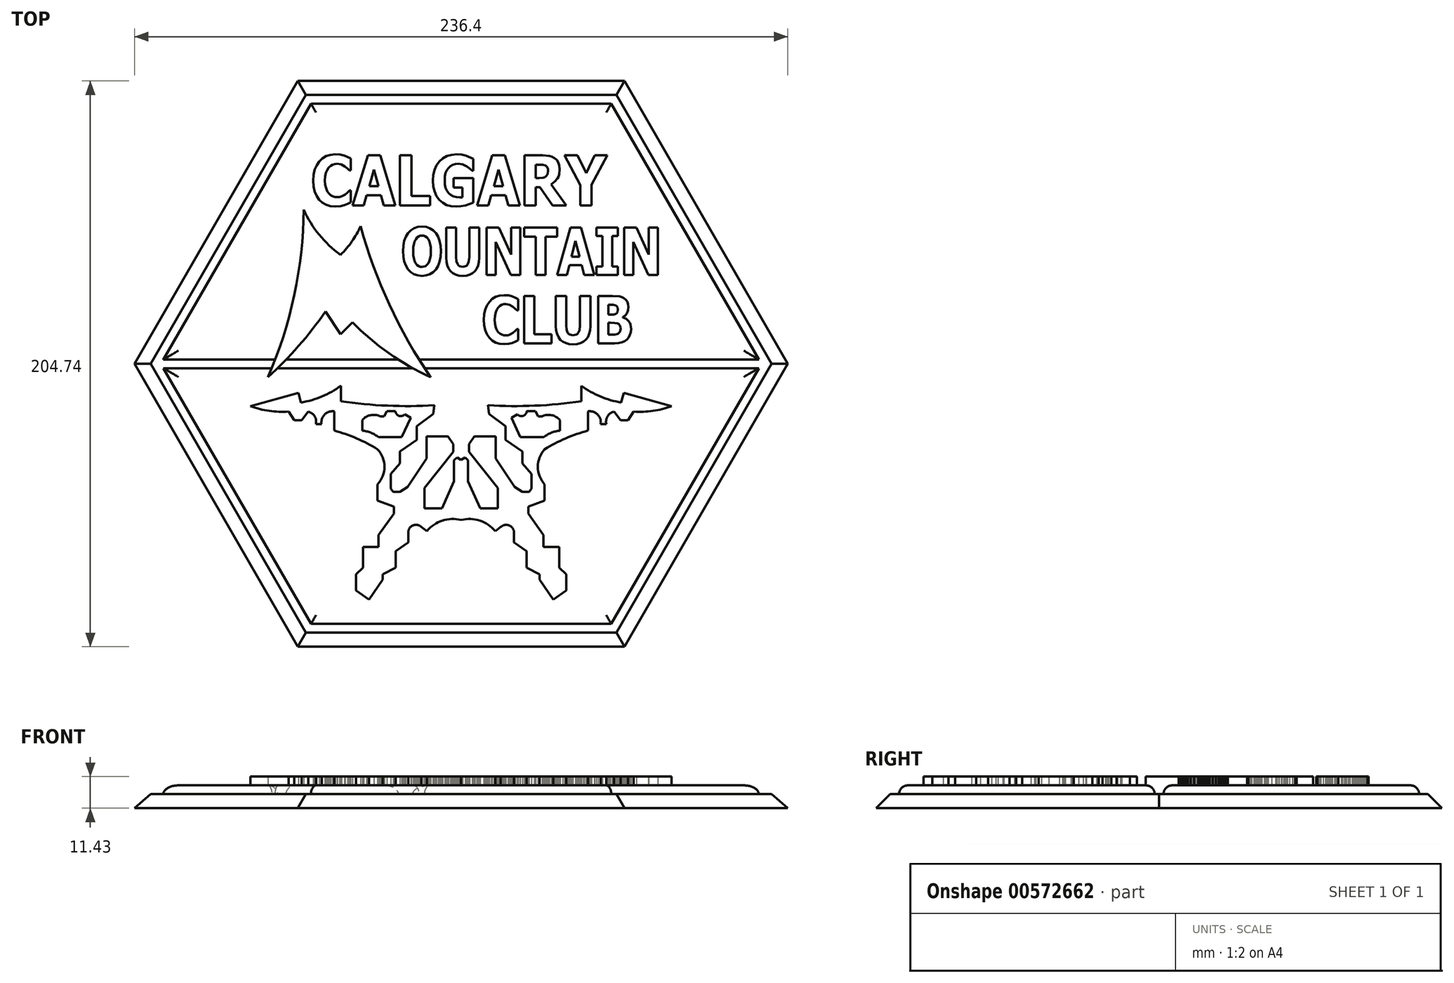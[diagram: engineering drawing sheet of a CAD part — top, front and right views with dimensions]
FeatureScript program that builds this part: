
annotation { "Feature Type Name" : "Feature", "Feature Type Description" : "" }
export const myFeature = defineFeature(function(context is Context, id is Id, definition is map)
    precondition{}
    {
        {
            var Q0;
            Q0=qCreatedBy(makeId("Top.planeOp"),FACE);
            var sketch = newSketch(context, id + "F0", { "sketchPlane" : qUnion([Q0])});
            skLineSegment(sketch, "E0", {"start": v(63.5, 109.99) * mm, "end": v(-63.5, 109.99) * mm});
            skLineSegment(sketch, "E1", {"start": v(63.5, 109.99) * mm, "end": v(127, 0) * mm});
            skLineSegment(sketch, "E2.1.0", {"start": v(-127, 0) * mm, "end": v(-63.5, 109.99) * mm});
            skLineSegment(sketch, "E2.1.1", {"start": v(-127, 0) * mm, "end": v(-63.5, -109.99) * mm});
            skLineSegment(sketch, "E2.2.0", {"start": v(63.5, -109.99) * mm, "end": v(-63.5, -109.99) * mm});
            skLineSegment(sketch, "E2.2.1", {"start": v(63.5, -109.99) * mm, "end": v(127, 0) * mm});
            skPoint(sketch, "E2.center", {"position": v(0, 0) * mm});
            skLineSegment(sketch, "E3", {"start": v(127, 0) * mm, "end": v(-127, 0) * mm, "construction": true});
            skSolve(sketch);
        }
        {
            var Q0;
            Q0=makeQuery(id+"F0.imprint","IMPRINT",FACE,{"disambiguationData":[TD([[makeQuery(id+"F0.imprint","IMPRINT",EDGE,{"derivedFrom":sQuery(id+"F0.wireOp",EDGE,"E0")}),1.0]])]});
            extrude(context, id + "F1", {"entities" : qUnion([Q0]), "depth" : 5.08 * mm, "offsetDistance" : 25.4 * mm});
        }
        {
            var Q0;
            Q0=makeQuery(id+"F1.opExtrude","CAP_EDGE",EDGE,{"disambiguationData":[OSD([sQuery(id+"F0.wireOp",EDGE,"E2.2.0")])],"isStart":false});
            var Q1;
            Q1=makeQuery(id+"F1.opExtrude","CAP_EDGE",EDGE,{"disambiguationData":[OSD([sQuery(id+"F0.wireOp",EDGE,"E2.1.1")])],"isStart":false});
            var Q2;
            Q2=makeQuery(id+"F1.opExtrude","CAP_EDGE",EDGE,{"disambiguationData":[OSD([sQuery(id+"F0.wireOp",EDGE,"E2.1.0")])],"isStart":false});
            var Q3;
            Q3=makeQuery(id+"F1.opExtrude","CAP_EDGE",EDGE,{"disambiguationData":[OSD([sQuery(id+"F0.wireOp",EDGE,"E0")])],"isStart":false});
            var Q4;
            Q4=makeQuery(id+"F1.opExtrude","CAP_EDGE",EDGE,{"disambiguationData":[OSD([sQuery(id+"F0.wireOp",EDGE,"E1")])],"isStart":false});
            var Q5;
            Q5=makeQuery(id+"F1.opExtrude","CAP_EDGE",EDGE,{"disambiguationData":[OSD([sQuery(id+"F0.wireOp",EDGE,"E2.2.1")])],"isStart":false});
            chamfer(context, id + "F2", {"entities" : qUnion([Q0, Q1, Q2, Q3, Q4, Q5]), "width" : 12.7 * mm, "tangentPropagation" : true});
        }
        {
            var Q0;
            Q0=makeQuery(id+"F1.opExtrude","CAP_FACE",FACE,{"disambiguationData":[OSD([sQuery(id+"F0.wireOp",EDGE,"E0"),sQuery(id+"F0.wireOp",EDGE,"E1"),sQuery(id+"F0.wireOp",EDGE,"E2.1.0"),sQuery(id+"F0.wireOp",EDGE,"E2.1.1"),sQuery(id+"F0.wireOp",EDGE,"E2.2.0"),sQuery(id+"F0.wireOp",EDGE,"E2.2.1")])],"isStart":false});
            var sketch = newSketch(context, id + "F3", { "sketchPlane" : qUnion([Q0])});
            skLineSegment(sketch, "E4.0", {"start": v(107.75, 1.59) * mm, "end": v(54.33, 94.11) * mm});
            skLineSegment(sketch, "E4.1", {"start": v(-54.33, 94.11) * mm, "end": v(-107.75, 1.59) * mm});
            skLineSegment(sketch, "E4.2", {"start": v(-107.75, -1.59) * mm, "end": v(-54.33, -94.11) * mm});
            skLineSegment(sketch, "E4.3", {"start": v(54.33, 94.11) * mm, "end": v(-54.33, 94.11) * mm});
            skLineSegment(sketch, "E4.4", {"start": v(-54.33, -94.11) * mm, "end": v(54.33, -94.11) * mm});
            skLineSegment(sketch, "E4.5", {"start": v(54.33, -94.11) * mm, "end": v(107.75, -1.59) * mm});
            skLineSegment(sketch, "E5", {"start": v(-112.31, 0) * mm, "end": v(112.31, 0) * mm, "construction": true});
            skLineSegment(sketch, "E6.0", {"start": v(-107.75, -1.59) * mm, "end": v(107.75, -1.59) * mm});
            skLineSegment(sketch, "E7.0", {"start": v(-107.75, 1.59) * mm, "end": v(107.75, 1.59) * mm});
            skLineSegment(sketch, "E8", {"start": v(0, -94.11) * mm, "end": v(0, 0) * mm, "construction": true});
            skSolve(sketch);
        }
        {
            var Q0;
            Q0=makeQuery(id+"F3.imprint","IMPRINT",FACE,{"disambiguationData":[TD([[makeQuery(id+"F3.imprint","IMPRINT",EDGE,{"derivedFrom":sQuery(id+"F3.wireOp",EDGE,"E4.2")}),1.0]])]});
            var Q1;
            Q1=makeQuery(id+"F3.imprint","IMPRINT",FACE,{"disambiguationData":[TD([[makeQuery(id+"F3.imprint","IMPRINT",EDGE,{"derivedFrom":sQuery(id+"F3.wireOp",EDGE,"E4.0")}),1.0]])]});
            extrude(context, id + "F4", {"entities" : qUnion([Q0, Q1]), "operationType" : NewBodyOperationType.ADD, "depth" : 3.17 * mm, "offsetDistance" : 25.4 * mm});
        }
        {
            var Q0;
            Q0=makeQuery(id+"F4.opExtrude","CAP_EDGE",EDGE,{"disambiguationData":[OSD([sQuery(id+"F3.wireOp",EDGE,"E6.0")])],"isStart":false});
            var Q1;
            Q1=makeQuery(id+"F4.opExtrude","CAP_EDGE",EDGE,{"disambiguationData":[OSD([sQuery(id+"F3.wireOp",EDGE,"E4.2")])],"isStart":false});
            var Q2;
            Q2=makeQuery(id+"F4.opExtrude","CAP_FACE",FACE,{"disambiguationData":[OSD([sQuery(id+"F3.wireOp",EDGE,"E4.2"),sQuery(id+"F3.wireOp",EDGE,"E4.4"),sQuery(id+"F3.wireOp",EDGE,"E4.5"),sQuery(id+"F3.wireOp",EDGE,"E6.0")])],"isStart":false});
            var Q3;
            Q3=makeQuery(id+"F4.opExtrude","CAP_FACE",FACE,{"disambiguationData":[OSD([sQuery(id+"F3.wireOp",EDGE,"E4.0"),sQuery(id+"F3.wireOp",EDGE,"E4.1"),sQuery(id+"F3.wireOp",EDGE,"E4.3"),sQuery(id+"F3.wireOp",EDGE,"E7.0")])],"isStart":false});
            fillet(context, id + "F5", {"entities" : qUnion([Q0, Q1, Q2, Q3]), "radius" : 3.17 * mm, "tangentPropagation" : true, "allowEdgeOverflow" : false});
        }
        {
            var Q0;
            Q0=makeQuery(id+"F4.opExtrude","CAP_FACE",FACE,{"disambiguationData":[OSD([sQuery(id+"F3.wireOp",EDGE,"E4.2"),sQuery(id+"F3.wireOp",EDGE,"E4.4"),sQuery(id+"F3.wireOp",EDGE,"E4.5"),sQuery(id+"F3.wireOp",EDGE,"E6.0")])],"isStart":false});
            var sketch = newSketch(context, id + "F6", { "sketchPlane" : qUnion([Q0])});
            skLineSegment(sketch, "E9", {"start": v(-43.55, 10.75) * mm, "end": v(-49.13, 18.93) * mm});
            skArc(sketch, "E10", {"start": v(-49.13, 18.93) * mm, "mid": v(-58.8, 6.48) * mm, "end": v(-69.85, -4.76) * mm});
            skArc(sketch, "E11", {"start": v(-69.85, -4.76) * mm, "mid": v(-60.37, 24.87) * mm, "end": v(-56.96, 55.8) * mm});
            skArc(sketch, "E12", {"start": v(-56.96, 55.8) * mm, "mid": v(-51.37, 46.74) * mm, "end": v(-43.62, 39.46) * mm});
            skArc(sketch, "E13", {"start": v(-36.39, 49.8) * mm, "mid": v(-39.52, 44.3) * mm, "end": v(-43.62, 39.46) * mm});
            skArc(sketch, "E14", {"start": v(-36.39, 49.8) * mm, "mid": v(-25.99, 21.46) * mm, "end": v(-11.07, -4.8) * mm});
            skArc(sketch, "E15", {"start": v(-11.07, -4.8) * mm, "mid": v(-26.11, 3.83) * mm, "end": v(-39.35, 15.04) * mm});
            skLineSegment(sketch, "E16", {"start": v(-39.35, 15.04) * mm, "end": v(-43.55, 10.75) * mm});
            skLineSegment(sketch, "E17", {"start": v(4.43, 58.3) * mm, "end": v(1.64, 57.34) * mm});
            skLineSegment(sketch, "E18", {"start": v(1.64, 57.34) * mm, "end": v(-0.07, 57) * mm});
            skLineSegment(sketch, "E19", {"start": v(-0.07, 57) * mm, "end": v(-1.76, 56.88) * mm});
            skLineSegment(sketch, "E20", {"start": v(-1.76, 56.88) * mm, "end": v(-3.59, 57.03) * mm});
            skLineSegment(sketch, "E21", {"start": v(-3.59, 57.03) * mm, "end": v(-5.22, 57.5) * mm});
            skLineSegment(sketch, "E22", {"start": v(-5.22, 57.5) * mm, "end": v(-6.66, 58.27) * mm});
            skLineSegment(sketch, "E23", {"start": v(-6.66, 58.27) * mm, "end": v(-7.9, 59.35) * mm});
            skLineSegment(sketch, "E24", {"start": v(-7.9, 59.35) * mm, "end": v(-8.9, 60.72) * mm});
            skLineSegment(sketch, "E25", {"start": v(-8.9, 60.72) * mm, "end": v(-9.63, 62.34) * mm});
            skLineSegment(sketch, "E26", {"start": v(-9.63, 62.34) * mm, "end": v(-10.06, 64.23) * mm});
            skLineSegment(sketch, "E27", {"start": v(-10.06, 64.23) * mm, "end": v(-10.2, 66.37) * mm});
            skLineSegment(sketch, "E28", {"start": v(-10.2, 66.37) * mm, "end": v(-10.06, 68.4) * mm});
            skLineSegment(sketch, "E29", {"start": v(-10.06, 68.4) * mm, "end": v(-9.63, 70.22) * mm});
            skLineSegment(sketch, "E30", {"start": v(-9.63, 70.22) * mm, "end": v(-8.9, 71.83) * mm});
            skLineSegment(sketch, "E31", {"start": v(-8.9, 71.83) * mm, "end": v(-7.9, 73.22) * mm});
            skLineSegment(sketch, "E32", {"start": v(-7.9, 73.22) * mm, "end": v(-6.65, 74.35) * mm});
            skLineSegment(sketch, "E33", {"start": v(-6.65, 74.35) * mm, "end": v(-5.2, 75.16) * mm});
            skLineSegment(sketch, "E34", {"start": v(-5.2, 75.16) * mm, "end": v(-3.52, 75.64) * mm});
            skLineSegment(sketch, "E35", {"start": v(-3.52, 75.64) * mm, "end": v(-1.63, 75.8) * mm});
            skLineSegment(sketch, "E36", {"start": v(-1.63, 75.8) * mm, "end": v(0.23, 75.7) * mm});
            skLineSegment(sketch, "E37", {"start": v(0.23, 75.7) * mm, "end": v(1.7, 75.37) * mm});
            skLineSegment(sketch, "E38", {"start": v(1.7, 75.37) * mm, "end": v(4.37, 74.19) * mm});
            skLineSegment(sketch, "E39", {"start": v(4.37, 74.19) * mm, "end": v(4.37, 69.92) * mm});
            skLineSegment(sketch, "E40", {"start": v(4.37, 69.92) * mm, "end": v(4, 69.92) * mm});
            skLineSegment(sketch, "E41", {"start": v(4, 69.92) * mm, "end": v(3.14, 70.65) * mm});
            skLineSegment(sketch, "E42", {"start": v(3.14, 70.65) * mm, "end": v(2.06, 71.45) * mm});
            skLineSegment(sketch, "E43", {"start": v(2.06, 71.45) * mm, "end": v(0.64, 72.12) * mm});
            skLineSegment(sketch, "E44", {"start": v(0.64, 72.12) * mm, "end": v(-0.2, 72.33) * mm});
            skLineSegment(sketch, "E45", {"start": v(-0.2, 72.33) * mm, "end": v(-1.07, 72.4) * mm});
            skLineSegment(sketch, "E46", {"start": v(-1.07, 72.4) * mm, "end": v(-2.08, 72.31) * mm});
            skLineSegment(sketch, "E47", {"start": v(-2.08, 72.31) * mm, "end": v(-3, 72.04) * mm});
            skLineSegment(sketch, "E48", {"start": v(-3, 72.04) * mm, "end": v(-3.82, 71.57) * mm});
            skLineSegment(sketch, "E49", {"start": v(-3.82, 71.57) * mm, "end": v(-4.55, 70.91) * mm});
            skLineSegment(sketch, "E50", {"start": v(-4.55, 70.91) * mm, "end": v(-5.13, 70.08) * mm});
            skLineSegment(sketch, "E51", {"start": v(-5.13, 70.08) * mm, "end": v(-5.58, 69.06) * mm});
            skLineSegment(sketch, "E52", {"start": v(-5.58, 69.06) * mm, "end": v(-5.86, 67.84) * mm});
            skLineSegment(sketch, "E53", {"start": v(-5.86, 67.84) * mm, "end": v(-5.96, 66.44) * mm});
            skLineSegment(sketch, "E54", {"start": v(-5.96, 66.44) * mm, "end": v(-5.87, 64.95) * mm});
            skLineSegment(sketch, "E55", {"start": v(-5.87, 64.95) * mm, "end": v(-5.6, 63.67) * mm});
            skLineSegment(sketch, "E56", {"start": v(-5.6, 63.67) * mm, "end": v(-5.14, 62.6) * mm});
            skLineSegment(sketch, "E57", {"start": v(-5.14, 62.6) * mm, "end": v(-4.51, 61.74) * mm});
            skLineSegment(sketch, "E58", {"start": v(-4.51, 61.74) * mm, "end": v(-3.73, 61.08) * mm});
            skLineSegment(sketch, "E59", {"start": v(-3.73, 61.08) * mm, "end": v(-2.81, 60.6) * mm});
            skLineSegment(sketch, "E60", {"start": v(-2.81, 60.6) * mm, "end": v(-1.76, 60.32) * mm});
            skLineSegment(sketch, "E61", {"start": v(-1.76, 60.32) * mm, "end": v(-0.58, 60.22) * mm});
            skLineSegment(sketch, "E62", {"start": v(-0.58, 60.22) * mm, "end": v(-0.06, 60.24) * mm});
            skLineSegment(sketch, "E63", {"start": v(-0.06, 60.24) * mm, "end": v(0.45, 60.27) * mm});
            skLineSegment(sketch, "E64", {"start": v(0.45, 60.27) * mm, "end": v(0.45, 63.84) * mm});
            skLineSegment(sketch, "E65", {"start": v(0.45, 63.84) * mm, "end": v(-2.72, 63.84) * mm});
            skLineSegment(sketch, "E66", {"start": v(-2.72, 63.84) * mm, "end": v(-2.72, 67.25) * mm});
            skLineSegment(sketch, "E67", {"start": v(-2.72, 67.25) * mm, "end": v(4.43, 67.25) * mm});
            skLineSegment(sketch, "E68", {"start": v(4.43, 67.25) * mm, "end": v(4.43, 58.3) * mm});
            skLineSegment(sketch, "E69", {"start": v(52.91, 75.45) * mm, "end": v(47.26, 64.85) * mm});
            skLineSegment(sketch, "E70", {"start": v(47.26, 64.85) * mm, "end": v(47.26, 57.26) * mm});
            skLineSegment(sketch, "E71", {"start": v(47.26, 57.26) * mm, "end": v(43.15, 57.26) * mm});
            skLineSegment(sketch, "E72", {"start": v(43.15, 57.26) * mm, "end": v(43.15, 64.62) * mm});
            skLineSegment(sketch, "E73", {"start": v(43.15, 64.62) * mm, "end": v(37.4, 75.45) * mm});
            skLineSegment(sketch, "E74", {"start": v(37.4, 75.45) * mm, "end": v(42.08, 75.45) * mm});
            skLineSegment(sketch, "E75", {"start": v(42.08, 75.45) * mm, "end": v(45.3, 68.95) * mm});
            skLineSegment(sketch, "E76", {"start": v(45.3, 68.95) * mm, "end": v(48.38, 75.45) * mm});
            skLineSegment(sketch, "E77", {"start": v(48.38, 75.45) * mm, "end": v(52.91, 75.45) * mm});
            skLineSegment(sketch, "E78", {"start": v(27.04, 63.93) * mm, "end": v(27.04, 57.26) * mm});
            skLineSegment(sketch, "E79", {"start": v(38.09, 57.26) * mm, "end": v(33.08, 57.26) * mm});
            skLineSegment(sketch, "E80", {"start": v(33.08, 57.26) * mm, "end": v(28.51, 63.93) * mm});
            skLineSegment(sketch, "E81", {"start": v(28.51, 63.93) * mm, "end": v(27.04, 63.93) * mm});
            skLineSegment(sketch, "E82", {"start": v(27.04, 57.26) * mm, "end": v(22.95, 57.26) * mm});
            skLineSegment(sketch, "E83", {"start": v(22.95, 57.26) * mm, "end": v(22.95, 75.45) * mm});
            skLineSegment(sketch, "E84", {"start": v(22.95, 75.45) * mm, "end": v(29.54, 75.45) * mm});
            skLineSegment(sketch, "E85", {"start": v(29.54, 75.45) * mm, "end": v(31.91, 75.26) * mm});
            skLineSegment(sketch, "E86", {"start": v(31.91, 75.26) * mm, "end": v(32.88, 74.96) * mm});
            skLineSegment(sketch, "E87", {"start": v(32.88, 74.96) * mm, "end": v(33.78, 74.47) * mm});
            skLineSegment(sketch, "E88", {"start": v(33.78, 74.47) * mm, "end": v(34.57, 73.76) * mm});
            skLineSegment(sketch, "E89", {"start": v(34.57, 73.76) * mm, "end": v(35.18, 72.89) * mm});
            skLineSegment(sketch, "E90", {"start": v(35.18, 72.89) * mm, "end": v(35.56, 71.8) * mm});
            skLineSegment(sketch, "E91", {"start": v(35.56, 71.8) * mm, "end": v(35.7, 70.45) * mm});
            skLineSegment(sketch, "E92", {"start": v(35.7, 70.45) * mm, "end": v(35.48, 68.56) * mm});
            skLineSegment(sketch, "E93", {"start": v(35.48, 68.56) * mm, "end": v(35.22, 67.76) * mm});
            skLineSegment(sketch, "E94", {"start": v(35.22, 67.76) * mm, "end": v(34.85, 67.06) * mm});
            skLineSegment(sketch, "E95", {"start": v(34.85, 67.06) * mm, "end": v(33.86, 65.9) * mm});
            skLineSegment(sketch, "E96", {"start": v(33.86, 65.9) * mm, "end": v(32.58, 64.99) * mm});
            skLineSegment(sketch, "E97", {"start": v(32.58, 64.99) * mm, "end": v(38.09, 57.26) * mm});
            skLineSegment(sketch, "E98", {"start": v(27.04, 72.1) * mm, "end": v(27.04, 67.2) * mm});
            skLineSegment(sketch, "E99", {"start": v(27.04, 67.2) * mm, "end": v(28.22, 67.2) * mm});
            skLineSegment(sketch, "E100", {"start": v(28.22, 67.2) * mm, "end": v(29.67, 67.32) * mm});
            skLineSegment(sketch, "E101", {"start": v(29.67, 67.32) * mm, "end": v(30.23, 67.5) * mm});
            skLineSegment(sketch, "E102", {"start": v(30.23, 67.5) * mm, "end": v(30.7, 67.81) * mm});
            skLineSegment(sketch, "E103", {"start": v(30.7, 67.81) * mm, "end": v(31.28, 68.63) * mm});
            skLineSegment(sketch, "E104", {"start": v(31.28, 68.63) * mm, "end": v(31.47, 69.88) * mm});
            skLineSegment(sketch, "E105", {"start": v(31.47, 69.88) * mm, "end": v(31.41, 70.51) * mm});
            skLineSegment(sketch, "E106", {"start": v(31.41, 70.51) * mm, "end": v(31.23, 71.05) * mm});
            skLineSegment(sketch, "E107", {"start": v(31.23, 71.05) * mm, "end": v(30.92, 71.5) * mm});
            skLineSegment(sketch, "E108", {"start": v(30.92, 71.5) * mm, "end": v(30.45, 71.82) * mm});
            skLineSegment(sketch, "E109", {"start": v(30.45, 71.82) * mm, "end": v(29.6, 72.05) * mm});
            skLineSegment(sketch, "E110", {"start": v(29.6, 72.05) * mm, "end": v(28.41, 72.1) * mm});
            skLineSegment(sketch, "E111", {"start": v(28.41, 72.1) * mm, "end": v(27.04, 72.1) * mm});
            skLineSegment(sketch, "E112", {"start": v(-39.96, 74.29) * mm, "end": v(-39.96, 69.95) * mm});
            skLineSegment(sketch, "E113", {"start": v(-39.96, 69.95) * mm, "end": v(-40.38, 69.95) * mm});
            skLineSegment(sketch, "E114", {"start": v(-40.38, 69.95) * mm, "end": v(-41.13, 70.65) * mm});
            skLineSegment(sketch, "E115", {"start": v(-41.13, 70.65) * mm, "end": v(-42.15, 71.45) * mm});
            skLineSegment(sketch, "E116", {"start": v(-42.15, 71.45) * mm, "end": v(-43.4, 72.12) * mm});
            skLineSegment(sketch, "E117", {"start": v(-43.4, 72.12) * mm, "end": v(-44.84, 72.4) * mm});
            skLineSegment(sketch, "E118", {"start": v(-44.84, 72.4) * mm, "end": v(-45.7, 72.31) * mm});
            skLineSegment(sketch, "E119", {"start": v(-45.7, 72.31) * mm, "end": v(-46.48, 72.08) * mm});
            skLineSegment(sketch, "E120", {"start": v(-46.48, 72.08) * mm, "end": v(-47.2, 71.65) * mm});
            skLineSegment(sketch, "E121", {"start": v(-47.2, 71.65) * mm, "end": v(-47.89, 71) * mm});
            skLineSegment(sketch, "E122", {"start": v(-47.89, 71) * mm, "end": v(-48.45, 70.18) * mm});
            skLineSegment(sketch, "E123", {"start": v(-48.45, 70.18) * mm, "end": v(-48.9, 69.12) * mm});
            skLineSegment(sketch, "E124", {"start": v(-48.9, 69.12) * mm, "end": v(-49.19, 67.83) * mm});
            skLineSegment(sketch, "E125", {"start": v(-49.19, 67.83) * mm, "end": v(-49.28, 66.32) * mm});
            skLineSegment(sketch, "E126", {"start": v(-49.28, 66.32) * mm, "end": v(-49.18, 64.76) * mm});
            skLineSegment(sketch, "E127", {"start": v(-49.18, 64.76) * mm, "end": v(-48.88, 63.47) * mm});
            skLineSegment(sketch, "E128", {"start": v(-48.88, 63.47) * mm, "end": v(-48.4, 62.42) * mm});
            skLineSegment(sketch, "E129", {"start": v(-48.4, 62.42) * mm, "end": v(-47.81, 61.6) * mm});
            skLineSegment(sketch, "E130", {"start": v(-47.81, 61.6) * mm, "end": v(-47.14, 61.02) * mm});
            skLineSegment(sketch, "E131", {"start": v(-47.14, 61.02) * mm, "end": v(-46.39, 60.62) * mm});
            skLineSegment(sketch, "E132", {"start": v(-46.39, 60.62) * mm, "end": v(-45.6, 60.39) * mm});
            skLineSegment(sketch, "E133", {"start": v(-45.6, 60.39) * mm, "end": v(-44.82, 60.31) * mm});
            skLineSegment(sketch, "E134", {"start": v(-44.82, 60.31) * mm, "end": v(-44.03, 60.38) * mm});
            skLineSegment(sketch, "E135", {"start": v(-44.03, 60.38) * mm, "end": v(-43.27, 60.6) * mm});
            skLineSegment(sketch, "E136", {"start": v(-43.27, 60.6) * mm, "end": v(-42.03, 61.28) * mm});
            skLineSegment(sketch, "E137", {"start": v(-42.03, 61.28) * mm, "end": v(-41.06, 62.04) * mm});
            skLineSegment(sketch, "E138", {"start": v(-41.06, 62.04) * mm, "end": v(-40.34, 62.74) * mm});
            skLineSegment(sketch, "E139", {"start": v(-40.34, 62.74) * mm, "end": v(-39.96, 62.74) * mm});
            skLineSegment(sketch, "E140", {"start": v(-39.96, 62.74) * mm, "end": v(-39.96, 58.47) * mm});
            skLineSegment(sketch, "E141", {"start": v(-39.96, 58.47) * mm, "end": v(-41, 57.93) * mm});
            skLineSegment(sketch, "E142", {"start": v(-41, 57.93) * mm, "end": v(-42.23, 57.43) * mm});
            skLineSegment(sketch, "E143", {"start": v(-42.23, 57.43) * mm, "end": v(-43.67, 57.04) * mm});
            skLineSegment(sketch, "E144", {"start": v(-43.67, 57.04) * mm, "end": v(-45.51, 56.9) * mm});
            skLineSegment(sketch, "E145", {"start": v(-45.51, 56.9) * mm, "end": v(-47.26, 57.06) * mm});
            skLineSegment(sketch, "E146", {"start": v(-47.26, 57.06) * mm, "end": v(-48.82, 57.52) * mm});
            skLineSegment(sketch, "E147", {"start": v(-48.82, 57.52) * mm, "end": v(-50.19, 58.3) * mm});
            skLineSegment(sketch, "E148", {"start": v(-50.19, 58.3) * mm, "end": v(-51.36, 59.38) * mm});
            skLineSegment(sketch, "E149", {"start": v(-51.36, 59.38) * mm, "end": v(-52.31, 60.74) * mm});
            skLineSegment(sketch, "E150", {"start": v(-52.31, 60.74) * mm, "end": v(-52.99, 62.35) * mm});
            skLineSegment(sketch, "E151", {"start": v(-52.99, 62.35) * mm, "end": v(-53.4, 64.22) * mm});
            skLineSegment(sketch, "E152", {"start": v(-53.4, 64.22) * mm, "end": v(-53.53, 66.33) * mm});
            skLineSegment(sketch, "E153", {"start": v(-53.53, 66.33) * mm, "end": v(-53.4, 68.39) * mm});
            skLineSegment(sketch, "E154", {"start": v(-53.4, 68.39) * mm, "end": v(-52.99, 70.22) * mm});
            skLineSegment(sketch, "E155", {"start": v(-52.99, 70.22) * mm, "end": v(-52.3, 71.83) * mm});
            skLineSegment(sketch, "E156", {"start": v(-52.3, 71.83) * mm, "end": v(-51.36, 73.23) * mm});
            skLineSegment(sketch, "E157", {"start": v(-51.36, 73.23) * mm, "end": v(-50.18, 74.35) * mm});
            skLineSegment(sketch, "E158", {"start": v(-50.18, 74.35) * mm, "end": v(-48.8, 75.16) * mm});
            skLineSegment(sketch, "E159", {"start": v(-48.8, 75.16) * mm, "end": v(-47.25, 75.64) * mm});
            skLineSegment(sketch, "E160", {"start": v(-47.25, 75.64) * mm, "end": v(-45.5, 75.8) * mm});
            skLineSegment(sketch, "E161", {"start": v(-45.5, 75.8) * mm, "end": v(-43.74, 75.68) * mm});
            skLineSegment(sketch, "E162", {"start": v(-43.74, 75.68) * mm, "end": v(-42.25, 75.34) * mm});
            skLineSegment(sketch, "E163", {"start": v(-42.25, 75.34) * mm, "end": v(-41.03, 74.84) * mm});
            skLineSegment(sketch, "E164", {"start": v(-41.03, 74.84) * mm, "end": v(-39.96, 74.29) * mm});
            skLineSegment(sketch, "E165", {"start": v(5.78, 57.26) * mm, "end": v(11.3, 75.45) * mm});
            skLineSegment(sketch, "E166", {"start": v(11.3, 75.45) * mm, "end": v(15.8, 75.45) * mm});
            skLineSegment(sketch, "E167", {"start": v(15.8, 75.45) * mm, "end": v(21.32, 57.26) * mm});
            skLineSegment(sketch, "E168", {"start": v(21.32, 57.26) * mm, "end": v(17.09, 57.26) * mm});
            skLineSegment(sketch, "E169", {"start": v(17.09, 57.26) * mm, "end": v(16.07, 60.97) * mm});
            skLineSegment(sketch, "E170", {"start": v(16.07, 60.97) * mm, "end": v(10.92, 60.97) * mm});
            skLineSegment(sketch, "E171", {"start": v(10.92, 60.97) * mm, "end": v(9.9, 57.26) * mm});
            skLineSegment(sketch, "E172", {"start": v(9.9, 57.26) * mm, "end": v(5.78, 57.26) * mm});
            skLineSegment(sketch, "E173", {"start": v(15.17, 64.27) * mm, "end": v(13.5, 70.27) * mm});
            skLineSegment(sketch, "E174", {"start": v(13.5, 70.27) * mm, "end": v(11.82, 64.27) * mm});
            skLineSegment(sketch, "E175", {"start": v(11.82, 64.27) * mm, "end": v(15.17, 64.27) * mm});
            skLineSegment(sketch, "E176", {"start": v(-11.2, 57.26) * mm, "end": v(-22.13, 57.26) * mm});
            skLineSegment(sketch, "E177", {"start": v(-22.13, 57.26) * mm, "end": v(-22.13, 75.45) * mm});
            skLineSegment(sketch, "E178", {"start": v(-22.13, 75.45) * mm, "end": v(-18.02, 75.45) * mm});
            skLineSegment(sketch, "E179", {"start": v(-18.02, 75.45) * mm, "end": v(-18.02, 60.73) * mm});
            skLineSegment(sketch, "E180", {"start": v(-18.02, 60.73) * mm, "end": v(-11.2, 60.73) * mm});
            skLineSegment(sketch, "E181", {"start": v(-11.2, 60.73) * mm, "end": v(-11.2, 57.26) * mm});
            skLineSegment(sketch, "E182", {"start": v(-39.3, 57.26) * mm, "end": v(-33.77, 75.45) * mm});
            skLineSegment(sketch, "E183", {"start": v(-33.77, 75.45) * mm, "end": v(-29.29, 75.45) * mm});
            skLineSegment(sketch, "E184", {"start": v(-29.29, 75.45) * mm, "end": v(-23.76, 57.26) * mm});
            skLineSegment(sketch, "E185", {"start": v(-23.76, 57.26) * mm, "end": v(-27.99, 57.26) * mm});
            skLineSegment(sketch, "E186", {"start": v(-27.99, 57.26) * mm, "end": v(-29.01, 60.97) * mm});
            skLineSegment(sketch, "E187", {"start": v(-29.01, 60.97) * mm, "end": v(-34.16, 60.97) * mm});
            skLineSegment(sketch, "E188", {"start": v(-34.16, 60.97) * mm, "end": v(-35.18, 57.26) * mm});
            skLineSegment(sketch, "E189", {"start": v(-35.18, 57.26) * mm, "end": v(-39.3, 57.26) * mm});
            skLineSegment(sketch, "E190", {"start": v(-29.91, 64.27) * mm, "end": v(-31.58, 70.27) * mm});
            skLineSegment(sketch, "E191", {"start": v(-31.58, 70.27) * mm, "end": v(-33.25, 64.27) * mm});
            skLineSegment(sketch, "E192", {"start": v(-33.25, 64.27) * mm, "end": v(-29.91, 64.27) * mm});
            skLineSegment(sketch, "E193", {"start": v(34.77, 49.3) * mm, "end": v(34.77, 46.03) * mm});
            skLineSegment(sketch, "E194", {"start": v(30.58, 46.03) * mm, "end": v(30.58, 32.2) * mm});
            skLineSegment(sketch, "E195", {"start": v(27.01, 32.2) * mm, "end": v(27.01, 46.03) * mm});
            skLineSegment(sketch, "E196", {"start": v(49.03, 49.3) * mm, "end": v(56.67, 49.3) * mm});
            skLineSegment(sketch, "E197", {"start": v(49.03, 32.2) * mm, "end": v(49.03, 35.18) * mm});
            skLineSegment(sketch, "E198", {"start": v(18.15, 39.5) * mm, "end": v(18.15, 49.3) * mm});
            skLineSegment(sketch, "E199", {"start": v(22.82, 46.03) * mm, "end": v(22.82, 49.3) * mm});
            skLineSegment(sketch, "E200", {"start": v(48.2, 32.2) * mm, "end": v(44.52, 32.2) * mm});
            skLineSegment(sketch, "E201", {"start": v(12.5, 32.2) * mm, "end": v(9.25, 32.2) * mm});
            skLineSegment(sketch, "E202", {"start": v(51.07, 46.3) * mm, "end": v(49.03, 46.3) * mm});
            skLineSegment(sketch, "E203", {"start": v(39.5, 49.3) * mm, "end": v(43.4, 49.3) * mm});
            skLineSegment(sketch, "E204", {"start": v(49.03, 46.3) * mm, "end": v(49.03, 49.3) * mm});
            skLineSegment(sketch, "E205", {"start": v(12.5, 44.11) * mm, "end": v(12.5, 32.2) * mm});
            skLineSegment(sketch, "E206", {"start": v(56.67, 32.2) * mm, "end": v(49.03, 32.2) * mm});
            skLineSegment(sketch, "E207", {"start": v(43.64, 35.69) * mm, "end": v(39.17, 35.69) * mm});
            skLineSegment(sketch, "E208", {"start": v(17.98, 32.2) * mm, "end": v(12.5, 44.11) * mm});
            skLineSegment(sketch, "E209", {"start": v(13.62, 49.3) * mm, "end": v(18.15, 39.5) * mm});
            skLineSegment(sketch, "E210", {"start": v(39.96, 38.79) * mm, "end": v(42.85, 38.79) * mm});
            skLineSegment(sketch, "E211", {"start": v(34.71, 32.2) * mm, "end": v(39.5, 49.3) * mm});
            skLineSegment(sketch, "E212", {"start": v(30.58, 32.2) * mm, "end": v(27.01, 32.2) * mm});
            skLineSegment(sketch, "E213", {"start": v(38.29, 32.2) * mm, "end": v(34.71, 32.2) * mm});
            skLineSegment(sketch, "E214", {"start": v(22.82, 49.3) * mm, "end": v(34.77, 49.3) * mm});
            skLineSegment(sketch, "E215", {"start": v(21.4, 32.2) * mm, "end": v(17.98, 32.2) * mm});
            skLineSegment(sketch, "E216", {"start": v(44.52, 32.2) * mm, "end": v(43.64, 35.69) * mm});
            skLineSegment(sketch, "E217", {"start": v(56.67, 49.3) * mm, "end": v(56.67, 46.3) * mm});
            skLineSegment(sketch, "E218", {"start": v(43.4, 49.3) * mm, "end": v(48.2, 32.2) * mm});
            skLineSegment(sketch, "E219", {"start": v(27.01, 46.03) * mm, "end": v(22.82, 46.03) * mm});
            skLineSegment(sketch, "E220", {"start": v(21.4, 49.3) * mm, "end": v(21.4, 32.2) * mm});
            skLineSegment(sketch, "E221", {"start": v(41.4, 44.42) * mm, "end": v(39.96, 38.79) * mm});
            skLineSegment(sketch, "E222", {"start": v(9.25, 49.3) * mm, "end": v(13.62, 49.3) * mm});
            skLineSegment(sketch, "E223", {"start": v(34.77, 46.03) * mm, "end": v(30.58, 46.03) * mm});
            skLineSegment(sketch, "E224", {"start": v(9.25, 32.2) * mm, "end": v(9.25, 49.3) * mm});
            skLineSegment(sketch, "E225", {"start": v(51.07, 35.18) * mm, "end": v(51.07, 46.3) * mm});
            skLineSegment(sketch, "E226", {"start": v(18.15, 49.3) * mm, "end": v(21.4, 49.3) * mm});
            skLineSegment(sketch, "E227", {"start": v(49.03, 35.18) * mm, "end": v(51.07, 35.18) * mm});
            skLineSegment(sketch, "E228", {"start": v(39.17, 35.69) * mm, "end": v(38.29, 32.2) * mm});
            skLineSegment(sketch, "E229", {"start": v(42.85, 38.79) * mm, "end": v(41.4, 44.42) * mm});
            skLineSegment(sketch, "E230", {"start": v(-18.2, 33.2) * mm, "end": v(-19.2, 34.24) * mm});
            skLineSegment(sketch, "E231", {"start": v(-19.2, 34.24) * mm, "end": v(-20, 35.55) * mm});
            skLineSegment(sketch, "E232", {"start": v(-20, 35.55) * mm, "end": v(-20.58, 37.07) * mm});
            skLineSegment(sketch, "E233", {"start": v(-20.58, 37.07) * mm, "end": v(-20.92, 38.8) * mm});
            skLineSegment(sketch, "E234", {"start": v(-20.92, 38.8) * mm, "end": v(-21.03, 40.74) * mm});
            skLineSegment(sketch, "E235", {"start": v(-21.03, 40.74) * mm, "end": v(-20.92, 42.7) * mm});
            skLineSegment(sketch, "E236", {"start": v(-20.92, 42.7) * mm, "end": v(-20.58, 44.43) * mm});
            skLineSegment(sketch, "E237", {"start": v(-20.58, 44.43) * mm, "end": v(-20, 45.95) * mm});
            skLineSegment(sketch, "E238", {"start": v(-20, 45.95) * mm, "end": v(-19.2, 47.26) * mm});
            skLineSegment(sketch, "E239", {"start": v(-19.2, 47.26) * mm, "end": v(-18.2, 48.3) * mm});
            skLineSegment(sketch, "E240", {"start": v(-18.2, 48.3) * mm, "end": v(-17.03, 49.05) * mm});
            skLineSegment(sketch, "E241", {"start": v(-17.03, 49.05) * mm, "end": v(-15.68, 49.5) * mm});
            skLineSegment(sketch, "E242", {"start": v(-15.68, 49.5) * mm, "end": v(-14.16, 49.65) * mm});
            skLineSegment(sketch, "E243", {"start": v(-14.16, 49.65) * mm, "end": v(-12.65, 49.5) * mm});
            skLineSegment(sketch, "E244", {"start": v(-12.65, 49.5) * mm, "end": v(-11.3, 49.05) * mm});
            skLineSegment(sketch, "E245", {"start": v(-11.3, 49.05) * mm, "end": v(-10.12, 48.3) * mm});
            skLineSegment(sketch, "E246", {"start": v(-10.12, 48.3) * mm, "end": v(-9.12, 47.27) * mm});
            skLineSegment(sketch, "E247", {"start": v(-9.12, 47.27) * mm, "end": v(-8.31, 45.97) * mm});
            skLineSegment(sketch, "E248", {"start": v(-8.31, 45.97) * mm, "end": v(-7.74, 44.44) * mm});
            skLineSegment(sketch, "E249", {"start": v(-7.74, 44.44) * mm, "end": v(-7.4, 42.7) * mm});
            skLineSegment(sketch, "E250", {"start": v(-7.4, 42.7) * mm, "end": v(-7.28, 40.74) * mm});
            skLineSegment(sketch, "E251", {"start": v(-7.28, 40.74) * mm, "end": v(-7.4, 38.78) * mm});
            skLineSegment(sketch, "E252", {"start": v(-7.4, 38.78) * mm, "end": v(-7.74, 37.04) * mm});
            skLineSegment(sketch, "E253", {"start": v(-7.74, 37.04) * mm, "end": v(-8.31, 35.51) * mm});
            skLineSegment(sketch, "E254", {"start": v(-8.31, 35.51) * mm, "end": v(-9.12, 34.22) * mm});
            skLineSegment(sketch, "E255", {"start": v(-9.12, 34.22) * mm, "end": v(-10.12, 33.18) * mm});
            skLineSegment(sketch, "E256", {"start": v(-10.12, 33.18) * mm, "end": v(-11.3, 32.43) * mm});
            skLineSegment(sketch, "E257", {"start": v(-11.3, 32.43) * mm, "end": v(-12.65, 31.99) * mm});
            skLineSegment(sketch, "E258", {"start": v(-12.65, 31.99) * mm, "end": v(-14.16, 31.84) * mm});
            skLineSegment(sketch, "E259", {"start": v(-14.16, 31.84) * mm, "end": v(-15.68, 31.99) * mm});
            skLineSegment(sketch, "E260", {"start": v(-15.68, 31.99) * mm, "end": v(-17.03, 32.44) * mm});
            skLineSegment(sketch, "E261", {"start": v(-17.03, 32.44) * mm, "end": v(-18.2, 33.2) * mm});
            skLineSegment(sketch, "E262", {"start": v(-5.37, 49.3) * mm, "end": v(-1.8, 49.3) * mm});
            skLineSegment(sketch, "E263", {"start": v(-1.8, 49.3) * mm, "end": v(-1.8, 38.63) * mm});
            skLineSegment(sketch, "E264", {"start": v(-1.8, 38.63) * mm, "end": v(-1.67, 37.07) * mm});
            skLineSegment(sketch, "E265", {"start": v(-1.67, 37.07) * mm, "end": v(-1.25, 35.97) * mm});
            skLineSegment(sketch, "E266", {"start": v(-1.25, 35.97) * mm, "end": v(-0.93, 35.6) * mm});
            skLineSegment(sketch, "E267", {"start": v(-0.93, 35.6) * mm, "end": v(-0.52, 35.32) * mm});
            skLineSegment(sketch, "E268", {"start": v(-0.52, 35.32) * mm, "end": v(0.56, 35.1) * mm});
            skLineSegment(sketch, "E269", {"start": v(0.56, 35.1) * mm, "end": v(1.63, 35.3) * mm});
            skLineSegment(sketch, "E270", {"start": v(1.63, 35.3) * mm, "end": v(2.04, 35.57) * mm});
            skLineSegment(sketch, "E271", {"start": v(2.04, 35.57) * mm, "end": v(2.37, 35.94) * mm});
            skLineSegment(sketch, "E272", {"start": v(2.37, 35.94) * mm, "end": v(2.8, 37.03) * mm});
            skLineSegment(sketch, "E273", {"start": v(2.8, 37.03) * mm, "end": v(2.95, 38.63) * mm});
            skLineSegment(sketch, "E274", {"start": v(2.95, 38.63) * mm, "end": v(2.95, 49.3) * mm});
            skLineSegment(sketch, "E275", {"start": v(2.95, 49.3) * mm, "end": v(6.51, 49.3) * mm});
            skLineSegment(sketch, "E276", {"start": v(6.51, 49.3) * mm, "end": v(6.51, 38.38) * mm});
            skLineSegment(sketch, "E277", {"start": v(6.51, 38.38) * mm, "end": v(6.42, 36.9) * mm});
            skLineSegment(sketch, "E278", {"start": v(6.42, 36.9) * mm, "end": v(6.14, 35.6) * mm});
            skLineSegment(sketch, "E279", {"start": v(6.14, 35.6) * mm, "end": v(5.67, 34.47) * mm});
            skLineSegment(sketch, "E280", {"start": v(5.67, 34.47) * mm, "end": v(5.01, 33.53) * mm});
            skLineSegment(sketch, "E281", {"start": v(5.01, 33.53) * mm, "end": v(4.17, 32.8) * mm});
            skLineSegment(sketch, "E282", {"start": v(4.17, 32.8) * mm, "end": v(3.15, 32.26) * mm});
            skLineSegment(sketch, "E283", {"start": v(3.15, 32.26) * mm, "end": v(1.95, 31.94) * mm});
            skLineSegment(sketch, "E284", {"start": v(1.95, 31.94) * mm, "end": v(0.56, 31.84) * mm});
            skLineSegment(sketch, "E285", {"start": v(0.56, 31.84) * mm, "end": v(-0.78, 31.94) * mm});
            skLineSegment(sketch, "E286", {"start": v(-0.78, 31.94) * mm, "end": v(-1.96, 32.26) * mm});
            skLineSegment(sketch, "E287", {"start": v(-1.96, 32.26) * mm, "end": v(-2.98, 32.78) * mm});
            skLineSegment(sketch, "E288", {"start": v(-2.98, 32.78) * mm, "end": v(-3.83, 33.5) * mm});
            skLineSegment(sketch, "E289", {"start": v(-3.83, 33.5) * mm, "end": v(-4.5, 34.43) * mm});
            skLineSegment(sketch, "E290", {"start": v(-4.5, 34.43) * mm, "end": v(-4.99, 35.55) * mm});
            skLineSegment(sketch, "E291", {"start": v(-4.99, 35.55) * mm, "end": v(-5.28, 36.87) * mm});
            skLineSegment(sketch, "E292", {"start": v(-5.28, 36.87) * mm, "end": v(-5.37, 38.37) * mm});
            skLineSegment(sketch, "E293", {"start": v(-5.37, 38.37) * mm, "end": v(-5.37, 49.3) * mm});
            skLineSegment(sketch, "E294", {"start": v(-14.76, 35.14) * mm, "end": v(-14.15, 35.07) * mm});
            skLineSegment(sketch, "E295", {"start": v(-14.15, 35.07) * mm, "end": v(-13.53, 35.15) * mm});
            skLineSegment(sketch, "E296", {"start": v(-13.53, 35.15) * mm, "end": v(-12.93, 35.4) * mm});
            skLineSegment(sketch, "E297", {"start": v(-12.93, 35.4) * mm, "end": v(-12.38, 35.81) * mm});
            skLineSegment(sketch, "E298", {"start": v(-12.38, 35.81) * mm, "end": v(-11.91, 36.4) * mm});
            skLineSegment(sketch, "E299", {"start": v(-11.91, 36.4) * mm, "end": v(-11.5, 37.22) * mm});
            skLineSegment(sketch, "E300", {"start": v(-11.5, 37.22) * mm, "end": v(-11.2, 38.15) * mm});
            skLineSegment(sketch, "E301", {"start": v(-11.2, 38.15) * mm, "end": v(-11.02, 39.3) * mm});
            skLineSegment(sketch, "E302", {"start": v(-11.02, 39.3) * mm, "end": v(-10.96, 40.75) * mm});
            skLineSegment(sketch, "E303", {"start": v(-10.96, 40.75) * mm, "end": v(-11.02, 42.16) * mm});
            skLineSegment(sketch, "E304", {"start": v(-11.02, 42.16) * mm, "end": v(-11.22, 43.35) * mm});
            skLineSegment(sketch, "E305", {"start": v(-11.22, 43.35) * mm, "end": v(-11.53, 44.33) * mm});
            skLineSegment(sketch, "E306", {"start": v(-11.53, 44.33) * mm, "end": v(-11.92, 45.11) * mm});
            skLineSegment(sketch, "E307", {"start": v(-11.92, 45.11) * mm, "end": v(-12.4, 45.71) * mm});
            skLineSegment(sketch, "E308", {"start": v(-12.4, 45.71) * mm, "end": v(-12.96, 46.12) * mm});
            skLineSegment(sketch, "E309", {"start": v(-12.96, 46.12) * mm, "end": v(-13.54, 46.35) * mm});
            skLineSegment(sketch, "E310", {"start": v(-13.54, 46.35) * mm, "end": v(-14.15, 46.42) * mm});
            skLineSegment(sketch, "E311", {"start": v(-14.15, 46.42) * mm, "end": v(-14.78, 46.35) * mm});
            skLineSegment(sketch, "E312", {"start": v(-14.78, 46.35) * mm, "end": v(-15.34, 46.14) * mm});
            skLineSegment(sketch, "E313", {"start": v(-15.34, 46.14) * mm, "end": v(-15.87, 45.75) * mm});
            skLineSegment(sketch, "E314", {"start": v(-15.87, 45.75) * mm, "end": v(-16.37, 45.14) * mm});
            skLineSegment(sketch, "E315", {"start": v(-16.37, 45.14) * mm, "end": v(-16.77, 44.36) * mm});
            skLineSegment(sketch, "E316", {"start": v(-16.77, 44.36) * mm, "end": v(-17.08, 43.37) * mm});
            skLineSegment(sketch, "E317", {"start": v(-17.08, 43.37) * mm, "end": v(-17.29, 42.16) * mm});
            skLineSegment(sketch, "E318", {"start": v(-17.29, 42.16) * mm, "end": v(-17.35, 40.74) * mm});
            skLineSegment(sketch, "E319", {"start": v(-17.35, 40.74) * mm, "end": v(-17.29, 39.3) * mm});
            skLineSegment(sketch, "E320", {"start": v(-17.29, 39.3) * mm, "end": v(-17.1, 38.13) * mm});
            skLineSegment(sketch, "E321", {"start": v(-17.1, 38.13) * mm, "end": v(-16.8, 37.17) * mm});
            skLineSegment(sketch, "E322", {"start": v(-16.8, 37.17) * mm, "end": v(-16.4, 36.39) * mm});
            skLineSegment(sketch, "E323", {"start": v(-16.4, 36.39) * mm, "end": v(-15.9, 35.78) * mm});
            skLineSegment(sketch, "E324", {"start": v(-15.9, 35.78) * mm, "end": v(-15.35, 35.37) * mm});
            skLineSegment(sketch, "E325", {"start": v(-15.35, 35.37) * mm, "end": v(-14.76, 35.14) * mm});
            skLineSegment(sketch, "E326", {"start": v(54.63, 35.18) * mm, "end": v(56.67, 35.18) * mm});
            skLineSegment(sketch, "E327", {"start": v(67.94, 39.5) * mm, "end": v(67.94, 49.3) * mm});
            skLineSegment(sketch, "E328", {"start": v(54.63, 46.3) * mm, "end": v(54.63, 35.18) * mm});
            skLineSegment(sketch, "E329", {"start": v(62.3, 32.2) * mm, "end": v(59.04, 32.2) * mm});
            skLineSegment(sketch, "E330", {"start": v(62.3, 44.11) * mm, "end": v(62.3, 32.2) * mm});
            skLineSegment(sketch, "E331", {"start": v(71.2, 49.3) * mm, "end": v(71.2, 32.2) * mm});
            skLineSegment(sketch, "E332", {"start": v(59.04, 32.2) * mm, "end": v(59.04, 49.3) * mm});
            skLineSegment(sketch, "E333", {"start": v(67.77, 32.2) * mm, "end": v(62.3, 44.11) * mm});
            skLineSegment(sketch, "E334", {"start": v(63.41, 49.3) * mm, "end": v(67.94, 39.5) * mm});
            skLineSegment(sketch, "E335", {"start": v(71.2, 32.2) * mm, "end": v(67.77, 32.2) * mm});
            skLineSegment(sketch, "E336", {"start": v(56.67, 46.3) * mm, "end": v(54.63, 46.3) * mm});
            skLineSegment(sketch, "E337", {"start": v(59.04, 49.3) * mm, "end": v(63.41, 49.3) * mm});
            skLineSegment(sketch, "E338", {"start": v(56.67, 35.18) * mm, "end": v(56.67, 32.2) * mm});
            skLineSegment(sketch, "E339", {"start": v(67.94, 49.3) * mm, "end": v(71.2, 49.3) * mm});
            skLineSegment(sketch, "E340", {"start": v(58.48, 16.88) * mm, "end": v(58.48, 16.79) * mm});
            skLineSegment(sketch, "E341", {"start": v(58.48, 16.79) * mm, "end": v(59.72, 16.28) * mm});
            skLineSegment(sketch, "E342", {"start": v(59.72, 16.28) * mm, "end": v(60.69, 15.43) * mm});
            skLineSegment(sketch, "E343", {"start": v(60.69, 15.43) * mm, "end": v(61.05, 14.87) * mm});
            skLineSegment(sketch, "E344", {"start": v(61.05, 14.87) * mm, "end": v(61.3, 14.22) * mm});
            skLineSegment(sketch, "E345", {"start": v(61.3, 14.22) * mm, "end": v(61.52, 12.65) * mm});
            skLineSegment(sketch, "E346", {"start": v(61.52, 12.65) * mm, "end": v(61.41, 11.46) * mm});
            skLineSegment(sketch, "E347", {"start": v(61.41, 11.46) * mm, "end": v(61.1, 10.41) * mm});
            skLineSegment(sketch, "E348", {"start": v(61.1, 10.41) * mm, "end": v(60.6, 9.53) * mm});
            skLineSegment(sketch, "E349", {"start": v(60.6, 9.53) * mm, "end": v(59.97, 8.82) * mm});
            skLineSegment(sketch, "E350", {"start": v(59.97, 8.82) * mm, "end": v(59.09, 8.17) * mm});
            skLineSegment(sketch, "E351", {"start": v(59.09, 8.17) * mm, "end": v(58.12, 7.74) * mm});
            skLineSegment(sketch, "E352", {"start": v(58.12, 7.74) * mm, "end": v(56.98, 7.5) * mm});
            skLineSegment(sketch, "E353", {"start": v(56.98, 7.5) * mm, "end": v(55.57, 7.42) * mm});
            skLineSegment(sketch, "E354", {"start": v(55.57, 7.42) * mm, "end": v(49.62, 7.42) * mm});
            skLineSegment(sketch, "E355", {"start": v(20.6, 23.42) * mm, "end": v(20.6, 19.35) * mm});
            skLineSegment(sketch, "E356", {"start": v(20.21, 19.35) * mm, "end": v(19.54, 20) * mm});
            skLineSegment(sketch, "E357", {"start": v(19.54, 20) * mm, "end": v(18.6, 20.76) * mm});
            skLineSegment(sketch, "E358", {"start": v(18.6, 20.76) * mm, "end": v(17.46, 21.39) * mm});
            skLineSegment(sketch, "E359", {"start": v(17.46, 21.39) * mm, "end": v(16.16, 21.64) * mm});
            skLineSegment(sketch, "E360", {"start": v(16.16, 21.64) * mm, "end": v(15.38, 21.57) * mm});
            skLineSegment(sketch, "E361", {"start": v(15.38, 21.57) * mm, "end": v(14.67, 21.35) * mm});
            skLineSegment(sketch, "E362", {"start": v(14.67, 21.35) * mm, "end": v(14.02, 20.95) * mm});
            skLineSegment(sketch, "E363", {"start": v(14.02, 20.95) * mm, "end": v(13.4, 20.34) * mm});
            skLineSegment(sketch, "E364", {"start": v(13.4, 20.34) * mm, "end": v(12.88, 19.57) * mm});
            skLineSegment(sketch, "E365", {"start": v(12.88, 19.57) * mm, "end": v(12.48, 18.57) * mm});
            skLineSegment(sketch, "E366", {"start": v(12.48, 18.57) * mm, "end": v(12.21, 17.35) * mm});
            skLineSegment(sketch, "E367", {"start": v(12.21, 17.35) * mm, "end": v(12.12, 15.94) * mm});
            skLineSegment(sketch, "E368", {"start": v(12.12, 15.94) * mm, "end": v(12.21, 14.47) * mm});
            skLineSegment(sketch, "E369", {"start": v(12.21, 14.47) * mm, "end": v(12.5, 13.26) * mm});
            skLineSegment(sketch, "E370", {"start": v(12.5, 13.26) * mm, "end": v(12.92, 12.28) * mm});
            skLineSegment(sketch, "E371", {"start": v(12.92, 12.28) * mm, "end": v(13.46, 11.5) * mm});
            skLineSegment(sketch, "E372", {"start": v(13.46, 11.5) * mm, "end": v(14.07, 10.95) * mm});
            skLineSegment(sketch, "E373", {"start": v(14.07, 10.95) * mm, "end": v(14.75, 10.57) * mm});
            skLineSegment(sketch, "E374", {"start": v(14.75, 10.57) * mm, "end": v(15.47, 10.36) * mm});
            skLineSegment(sketch, "E375", {"start": v(15.47, 10.36) * mm, "end": v(16.18, 10.29) * mm});
            skLineSegment(sketch, "E376", {"start": v(16.18, 10.29) * mm, "end": v(16.9, 10.36) * mm});
            skLineSegment(sketch, "E377", {"start": v(16.9, 10.36) * mm, "end": v(17.59, 10.57) * mm});
            skLineSegment(sketch, "E378", {"start": v(17.59, 10.57) * mm, "end": v(18.72, 11.2) * mm});
            skLineSegment(sketch, "E379", {"start": v(18.72, 11.2) * mm, "end": v(19.6, 11.92) * mm});
            skLineSegment(sketch, "E380", {"start": v(19.6, 11.92) * mm, "end": v(20.25, 12.57) * mm});
            skLineSegment(sketch, "E381", {"start": v(20.6, 19.35) * mm, "end": v(20.21, 19.35) * mm});
            skLineSegment(sketch, "E382", {"start": v(46.75, 24.52) * mm, "end": v(46.75, 13.6) * mm});
            skLineSegment(sketch, "E383", {"start": v(46.75, 13.6) * mm, "end": v(46.65, 12.12) * mm});
            skLineSegment(sketch, "E384", {"start": v(46.65, 12.12) * mm, "end": v(46.36, 10.81) * mm});
            skLineSegment(sketch, "E385", {"start": v(46.36, 10.81) * mm, "end": v(45.86, 9.7) * mm});
            skLineSegment(sketch, "E386", {"start": v(45.86, 9.7) * mm, "end": v(45.18, 8.75) * mm});
            skLineSegment(sketch, "E387", {"start": v(45.18, 8.75) * mm, "end": v(44.3, 8.01) * mm});
            skLineSegment(sketch, "E388", {"start": v(44.3, 8.01) * mm, "end": v(43.22, 7.48) * mm});
            skLineSegment(sketch, "E389", {"start": v(43.22, 7.48) * mm, "end": v(41.96, 7.17) * mm});
            skLineSegment(sketch, "E390", {"start": v(41.96, 7.17) * mm, "end": v(40.52, 7.06) * mm});
            skLineSegment(sketch, "E391", {"start": v(40.52, 7.06) * mm, "end": v(39.1, 7.16) * mm});
            skLineSegment(sketch, "E392", {"start": v(39.1, 7.16) * mm, "end": v(37.86, 7.48) * mm});
            skLineSegment(sketch, "E393", {"start": v(37.86, 7.48) * mm, "end": v(36.8, 8) * mm});
            skLineSegment(sketch, "E394", {"start": v(36.8, 8) * mm, "end": v(35.9, 8.73) * mm});
            skLineSegment(sketch, "E395", {"start": v(35.9, 8.73) * mm, "end": v(35.2, 9.65) * mm});
            skLineSegment(sketch, "E396", {"start": v(35.2, 9.65) * mm, "end": v(34.7, 10.78) * mm});
            skLineSegment(sketch, "E397", {"start": v(34.7, 10.78) * mm, "end": v(34.4, 12.09) * mm});
            skLineSegment(sketch, "E398", {"start": v(34.4, 12.09) * mm, "end": v(34.3, 13.6) * mm});
            skLineSegment(sketch, "E399", {"start": v(34.3, 13.6) * mm, "end": v(34.3, 24.52) * mm});
            skLineSegment(sketch, "E400", {"start": v(38.03, 24.52) * mm, "end": v(38.03, 13.85) * mm});
            skLineSegment(sketch, "E401", {"start": v(38.03, 13.85) * mm, "end": v(38.17, 12.3) * mm});
            skLineSegment(sketch, "E402", {"start": v(38.17, 12.3) * mm, "end": v(38.61, 11.2) * mm});
            skLineSegment(sketch, "E403", {"start": v(38.61, 11.2) * mm, "end": v(38.95, 10.81) * mm});
            skLineSegment(sketch, "E404", {"start": v(38.95, 10.81) * mm, "end": v(39.38, 10.54) * mm});
            skLineSegment(sketch, "E405", {"start": v(39.38, 10.54) * mm, "end": v(40.52, 10.32) * mm});
            skLineSegment(sketch, "E406", {"start": v(40.52, 10.32) * mm, "end": v(41.63, 10.53) * mm});
            skLineSegment(sketch, "E407", {"start": v(41.63, 10.53) * mm, "end": v(42.06, 10.8) * mm});
            skLineSegment(sketch, "E408", {"start": v(42.06, 10.8) * mm, "end": v(42.4, 11.16) * mm});
            skLineSegment(sketch, "E409", {"start": v(42.4, 11.16) * mm, "end": v(42.86, 12.25) * mm});
            skLineSegment(sketch, "E410", {"start": v(42.86, 12.25) * mm, "end": v(43.01, 13.85) * mm});
            skLineSegment(sketch, "E411", {"start": v(43.01, 13.85) * mm, "end": v(43.01, 24.52) * mm});
            skLineSegment(sketch, "E412", {"start": v(34.3, 24.52) * mm, "end": v(38.03, 24.52) * mm});
            skLineSegment(sketch, "E413", {"start": v(43.01, 24.52) * mm, "end": v(46.75, 24.52) * mm});
            skLineSegment(sketch, "E414", {"start": v(26.53, 24.52) * mm, "end": v(26.53, 10.68) * mm});
            skLineSegment(sketch, "E415", {"start": v(20.6, 12.57) * mm, "end": v(20.6, 8.55) * mm});
            skLineSegment(sketch, "E416", {"start": v(20.25, 12.57) * mm, "end": v(20.6, 12.57) * mm});
            skLineSegment(sketch, "E417", {"start": v(22.8, 24.52) * mm, "end": v(26.53, 24.52) * mm});
            skLineSegment(sketch, "E418", {"start": v(22.8, 7.42) * mm, "end": v(22.8, 24.52) * mm});
            skLineSegment(sketch, "E419", {"start": v(20.6, 8.55) * mm, "end": v(19.65, 8.05) * mm});
            skLineSegment(sketch, "E420", {"start": v(19.65, 8.05) * mm, "end": v(18.54, 7.58) * mm});
            skLineSegment(sketch, "E421", {"start": v(18.54, 7.58) * mm, "end": v(17.23, 7.21) * mm});
            skLineSegment(sketch, "E422", {"start": v(17.23, 7.21) * mm, "end": v(15.55, 7.08) * mm});
            skLineSegment(sketch, "E423", {"start": v(15.55, 7.08) * mm, "end": v(13.96, 7.23) * mm});
            skLineSegment(sketch, "E424", {"start": v(13.96, 7.23) * mm, "end": v(12.55, 7.67) * mm});
            skLineSegment(sketch, "E425", {"start": v(12.55, 7.67) * mm, "end": v(11.3, 8.4) * mm});
            skLineSegment(sketch, "E426", {"start": v(11.3, 8.4) * mm, "end": v(10.23, 9.4) * mm});
            skLineSegment(sketch, "E427", {"start": v(10.23, 9.4) * mm, "end": v(9.37, 10.69) * mm});
            skLineSegment(sketch, "E428", {"start": v(9.37, 10.69) * mm, "end": v(8.76, 12.2) * mm});
            skLineSegment(sketch, "E429", {"start": v(8.76, 12.2) * mm, "end": v(8.39, 13.96) * mm});
            skLineSegment(sketch, "E430", {"start": v(8.39, 13.96) * mm, "end": v(8.27, 15.95) * mm});
            skLineSegment(sketch, "E431", {"start": v(8.27, 15.95) * mm, "end": v(8.39, 17.88) * mm});
            skLineSegment(sketch, "E432", {"start": v(8.39, 17.88) * mm, "end": v(8.76, 19.6) * mm});
            skLineSegment(sketch, "E433", {"start": v(8.76, 19.6) * mm, "end": v(9.38, 21.12) * mm});
            skLineSegment(sketch, "E434", {"start": v(9.38, 21.12) * mm, "end": v(10.24, 22.43) * mm});
            skLineSegment(sketch, "E435", {"start": v(10.24, 22.43) * mm, "end": v(11.31, 23.49) * mm});
            skLineSegment(sketch, "E436", {"start": v(11.31, 23.49) * mm, "end": v(12.56, 24.24) * mm});
            skLineSegment(sketch, "E437", {"start": v(12.56, 24.24) * mm, "end": v(13.97, 24.7) * mm});
            skLineSegment(sketch, "E438", {"start": v(13.97, 24.7) * mm, "end": v(15.56, 24.85) * mm});
            skLineSegment(sketch, "E439", {"start": v(15.56, 24.85) * mm, "end": v(17.16, 24.73) * mm});
            skLineSegment(sketch, "E440", {"start": v(17.16, 24.73) * mm, "end": v(18.52, 24.41) * mm});
            skLineSegment(sketch, "E441", {"start": v(18.52, 24.41) * mm, "end": v(19.63, 23.94) * mm});
            skLineSegment(sketch, "E442", {"start": v(19.63, 23.94) * mm, "end": v(20.6, 23.42) * mm});
            skLineSegment(sketch, "E443", {"start": v(26.53, 10.68) * mm, "end": v(32.72, 10.68) * mm});
            skLineSegment(sketch, "E444", {"start": v(32.72, 10.68) * mm, "end": v(32.72, 7.42) * mm});
            skLineSegment(sketch, "E445", {"start": v(32.72, 7.42) * mm, "end": v(22.8, 7.42) * mm});
            skLineSegment(sketch, "E446", {"start": v(49.62, 24.52) * mm, "end": v(54.87, 24.52) * mm});
            skLineSegment(sketch, "E447", {"start": v(54.87, 24.52) * mm, "end": v(57.35, 24.37) * mm});
            skLineSegment(sketch, "E448", {"start": v(57.35, 24.37) * mm, "end": v(58.17, 24.15) * mm});
            skLineSegment(sketch, "E449", {"start": v(58.17, 24.15) * mm, "end": v(58.94, 23.77) * mm});
            skLineSegment(sketch, "E450", {"start": v(58.94, 23.77) * mm, "end": v(59.64, 23.2) * mm});
            skLineSegment(sketch, "E451", {"start": v(59.64, 23.2) * mm, "end": v(60.13, 22.45) * mm});
            skLineSegment(sketch, "E452", {"start": v(60.13, 22.45) * mm, "end": v(60.43, 21.56) * mm});
            skLineSegment(sketch, "E453", {"start": v(60.43, 21.56) * mm, "end": v(60.53, 20.54) * mm});
            skLineSegment(sketch, "E454", {"start": v(60.53, 20.54) * mm, "end": v(60.39, 19.36) * mm});
            skLineSegment(sketch, "E455", {"start": v(60.39, 19.36) * mm, "end": v(59.98, 18.31) * mm});
            skLineSegment(sketch, "E456", {"start": v(59.98, 18.31) * mm, "end": v(59.33, 17.47) * mm});
            skLineSegment(sketch, "E457", {"start": v(59.33, 17.47) * mm, "end": v(58.48, 16.88) * mm});
            skLineSegment(sketch, "E458", {"start": v(49.62, 7.42) * mm, "end": v(49.62, 24.52) * mm});
            skLineSegment(sketch, "E459", {"start": v(53.33, 21.38) * mm, "end": v(53.33, 17.76) * mm});
            skLineSegment(sketch, "E460", {"start": v(53.33, 17.76) * mm, "end": v(53.8, 17.76) * mm});
            skLineSegment(sketch, "E461", {"start": v(53.8, 17.76) * mm, "end": v(55.15, 17.79) * mm});
            skLineSegment(sketch, "E462", {"start": v(55.15, 17.79) * mm, "end": v(55.94, 18.03) * mm});
            skLineSegment(sketch, "E463", {"start": v(55.94, 18.03) * mm, "end": v(56.32, 18.31) * mm});
            skLineSegment(sketch, "E464", {"start": v(56.32, 18.31) * mm, "end": v(56.56, 18.7) * mm});
            skLineSegment(sketch, "E465", {"start": v(56.56, 18.7) * mm, "end": v(56.73, 19.68) * mm});
            skLineSegment(sketch, "E466", {"start": v(56.73, 19.68) * mm, "end": v(56.54, 20.53) * mm});
            skLineSegment(sketch, "E467", {"start": v(56.54, 20.53) * mm, "end": v(56.3, 20.9) * mm});
            skLineSegment(sketch, "E468", {"start": v(56.3, 20.9) * mm, "end": v(55.97, 21.16) * mm});
            skLineSegment(sketch, "E469", {"start": v(55.97, 21.16) * mm, "end": v(55.1, 21.36) * mm});
            skLineSegment(sketch, "E470", {"start": v(55.1, 21.36) * mm, "end": v(53.6, 21.38) * mm});
            skLineSegment(sketch, "E471", {"start": v(53.6, 21.38) * mm, "end": v(53.33, 21.38) * mm});
            skLineSegment(sketch, "E472", {"start": v(53.33, 14.84) * mm, "end": v(53.33, 10.55) * mm});
            skLineSegment(sketch, "E473", {"start": v(53.33, 10.55) * mm, "end": v(53.53, 10.55) * mm});
            skLineSegment(sketch, "E474", {"start": v(53.53, 10.55) * mm, "end": v(55.55, 10.57) * mm});
            skLineSegment(sketch, "E475", {"start": v(55.55, 10.57) * mm, "end": v(56.69, 10.88) * mm});
            skLineSegment(sketch, "E476", {"start": v(56.69, 10.88) * mm, "end": v(57.13, 11.2) * mm});
            skLineSegment(sketch, "E477", {"start": v(57.13, 11.2) * mm, "end": v(57.43, 11.63) * mm});
            skLineSegment(sketch, "E478", {"start": v(57.43, 11.63) * mm, "end": v(57.6, 12.15) * mm});
            skLineSegment(sketch, "E479", {"start": v(57.6, 12.15) * mm, "end": v(57.67, 12.73) * mm});
            skLineSegment(sketch, "E480", {"start": v(57.67, 12.73) * mm, "end": v(57.6, 13.44) * mm});
            skLineSegment(sketch, "E481", {"start": v(57.6, 13.44) * mm, "end": v(57.39, 13.97) * mm});
            skLineSegment(sketch, "E482", {"start": v(57.39, 13.97) * mm, "end": v(57.04, 14.37) * mm});
            skLineSegment(sketch, "E483", {"start": v(57.04, 14.37) * mm, "end": v(56.55, 14.65) * mm});
            skLineSegment(sketch, "E484", {"start": v(56.55, 14.65) * mm, "end": v(55.62, 14.82) * mm});
            skLineSegment(sketch, "E485", {"start": v(55.62, 14.82) * mm, "end": v(54.02, 14.84) * mm});
            skLineSegment(sketch, "E486", {"start": v(54.02, 14.84) * mm, "end": v(53.33, 14.84) * mm});
            skArc(sketch, "E487", {"start": v(9.72, -15) * mm, "mid": v(26.66, -15.14) * mm, "end": v(43.52, -13.51) * mm});
            skLineSegment(sketch, "E488", {"start": v(43.52, -13.51) * mm, "end": v(43.52, -7.97) * mm});
            skArc(sketch, "E489", {"start": v(43.52, -7.97) * mm, "mid": v(50.37, -11.82) * mm, "end": v(57.92, -14) * mm});
            skLineSegment(sketch, "E490", {"start": v(57.92, -14) * mm, "end": v(58.87, -10.56) * mm});
            skLineSegment(sketch, "E491", {"start": v(58.87, -10.56) * mm, "end": v(76.2, -15.34) * mm});
            skArc(sketch, "E492", {"start": v(76.2, -15.34) * mm, "mid": v(69.43, -17.02) * mm, "end": v(62.45, -17.28) * mm});
            skArc(sketch, "E493", {"start": v(55.36, -17.28) * mm, "mid": v(53, -18.99) * mm, "end": v(52.56, -21.87) * mm});
            skArc(sketch, "E494", {"start": v(50.5, -21.87) * mm, "mid": v(49.39, -18.35) * mm, "end": v(45.89, -17.18) * mm});
            skLineSegment(sketch, "E495", {"start": v(45.89, -17.18) * mm, "end": v(45.89, -24.16) * mm});
            skLineSegment(sketch, "E496", {"start": v(21.46, -26.55) * mm, "end": v(29.93, -26.55) * mm});
            skLineSegment(sketch, "E497", {"start": v(18.27, -19.5) * mm, "end": v(21.46, -26.55) * mm});
            skLineSegment(sketch, "E498", {"start": v(29.84, -66.22) * mm, "end": v(35.52, -66.22) * mm});
            skLineSegment(sketch, "E499", {"start": v(24.3, -51.69) * mm, "end": v(24.3, -54.15) * mm});
            skArc(sketch, "E500", {"start": v(45.89, -24.16) * mm, "mid": v(37.82, -26.99) * mm, "end": v(30.23, -30.92) * mm});
            skLineSegment(sketch, "E501", {"start": v(57.69, -20.46) * mm, "end": v(55.36, -17.28) * mm});
            skLineSegment(sketch, "E502", {"start": v(50.5, -21.87) * mm, "end": v(52.56, -21.87) * mm});
            skLineSegment(sketch, "E503", {"start": v(62.45, -17.28) * mm, "end": v(60.38, -20.46) * mm});
            skLineSegment(sketch, "E504", {"start": v(60.38, -20.46) * mm, "end": v(57.69, -20.46) * mm});
            skArc(sketch, "E505", {"start": v(30.23, -30.92) * mm, "mid": v(27.76, -37.27) * mm, "end": v(30.23, -43.62) * mm});
            skLineSegment(sketch, "E506", {"start": v(30.23, -43.62) * mm, "end": v(30.23, -49.55) * mm});
            skLineSegment(sketch, "E507", {"start": v(30.23, -49.55) * mm, "end": v(24.3, -51.69) * mm});
            skArc(sketch, "E508", {"start": v(12.38, -60.6) * mm, "mid": v(6.8, -56.73) * mm, "end": v(0, -56.53) * mm});
            skLineSegment(sketch, "E509", {"start": v(29.84, -61.92) * mm, "end": v(29.84, -66.22) * mm});
            skLineSegment(sketch, "E510", {"start": v(24.3, -54.15) * mm, "end": v(29.84, -61.92) * mm});
            skLineSegment(sketch, "E511", {"start": v(35.52, -73.8) * mm, "end": v(38, -76.22) * mm});
            skLineSegment(sketch, "E512", {"start": v(35.52, -66.22) * mm, "end": v(35.52, -73.8) * mm});
            skLineSegment(sketch, "E513", {"start": v(12.38, -60.6) * mm, "end": v(14.35, -59.08) * mm});
            skLineSegment(sketch, "E514", {"start": v(38, -76.22) * mm, "end": v(38, -82.06) * mm});
            skLineSegment(sketch, "E515", {"start": v(38, -82.06) * mm, "end": v(33.38, -85.3) * mm});
            skLineSegment(sketch, "E516", {"start": v(28.35, -76.22) * mm, "end": v(23.69, -73.76) * mm});
            skLineSegment(sketch, "E517", {"start": v(19.36, -44.6) * mm, "end": v(22.14, -46.35) * mm});
            skLineSegment(sketch, "E518", {"start": v(28.35, -78.13) * mm, "end": v(28.35, -76.22) * mm});
            skLineSegment(sketch, "E519", {"start": v(33.38, -85.3) * mm, "end": v(28.35, -78.13) * mm});
            skLineSegment(sketch, "E520", {"start": v(23.69, -67.83) * mm, "end": v(19.15, -64.6) * mm});
            skLineSegment(sketch, "E521", {"start": v(23.69, -73.76) * mm, "end": v(23.69, -72.14) * mm});
            skLineSegment(sketch, "E522", {"start": v(24.6, -46.35) * mm, "end": v(25.51, -45.15) * mm});
            skLineSegment(sketch, "E523", {"start": v(13.24, -52.3) * mm, "end": v(13.24, -44.96) * mm});
            skArc(sketch, "E524", {"start": v(14.35, -59.08) * mm, "mid": v(17.41, -58.47) * mm, "end": v(19.15, -61.07) * mm});
            skLineSegment(sketch, "E525", {"start": v(23.69, -72.14) * mm, "end": v(23.69, -67.83) * mm});
            skLineSegment(sketch, "E526", {"start": v(19.15, -64.6) * mm, "end": v(19.15, -61.07) * mm});
            skLineSegment(sketch, "E527", {"start": v(6.9, -52.3) * mm, "end": v(13.24, -52.3) * mm});
            skLineSegment(sketch, "E528", {"start": v(0, -34.76) * mm, "end": v(1.43, -33.9) * mm});
            skLineSegment(sketch, "E529", {"start": v(2.53, -42.5) * mm, "end": v(6.9, -52.3) * mm});
            skLineSegment(sketch, "E530", {"start": v(1.43, -33.9) * mm, "end": v(2.53, -34.89) * mm});
            skLineSegment(sketch, "E531", {"start": v(2.9, -31.88) * mm, "end": v(2.9, -29.05) * mm});
            skLineSegment(sketch, "E532", {"start": v(2.53, -34.89) * mm, "end": v(2.53, -42.5) * mm});
            skLineSegment(sketch, "E533", {"start": v(22.14, -46.35) * mm, "end": v(24.6, -46.35) * mm});
            skLineSegment(sketch, "E534", {"start": v(13.24, -44.96) * mm, "end": v(2.9, -31.88) * mm});
            skLineSegment(sketch, "E535", {"start": v(4.73, -26.3) * mm, "end": v(12.5, -26.3) * mm});
            skLineSegment(sketch, "E536", {"start": v(2.9, -29.05) * mm, "end": v(4.73, -26.3) * mm});
            skLineSegment(sketch, "E537", {"start": v(12.5, -34.26) * mm, "end": v(19.36, -44.6) * mm});
            skLineSegment(sketch, "E538", {"start": v(12.5, -26.3) * mm, "end": v(12.5, -34.26) * mm});
            skLineSegment(sketch, "E539", {"start": v(25.51, -45.15) * mm, "end": v(25.51, -39.91) * mm});
            skLineSegment(sketch, "E540", {"start": v(25.51, -39.91) * mm, "end": v(22.21, -36.09) * mm});
            skLineSegment(sketch, "E541", {"start": v(22.21, -36.09) * mm, "end": v(22.21, -31.67) * mm});
            skLineSegment(sketch, "E542", {"start": v(16.06, -27.48) * mm, "end": v(16.06, -22.6) * mm});
            skLineSegment(sketch, "E543", {"start": v(22.21, -31.67) * mm, "end": v(16.06, -27.48) * mm});
            skLineSegment(sketch, "E544", {"start": v(10.12, -18.13) * mm, "end": v(9.72, -15) * mm});
            skLineSegment(sketch, "E545", {"start": v(16.06, -22.6) * mm, "end": v(10.12, -18.13) * mm});
            skLineSegment(sketch, "E546", {"start": v(26.83, -17.13) * mm, "end": v(23.78, -17.13) * mm});
            skLineSegment(sketch, "E547", {"start": v(35.8, -24.2) * mm, "end": v(35.8, -20.36) * mm});
            skArc(sketch, "E548", {"start": v(35.8, -20.36) * mm, "mid": v(32.8, -18.58) * mm, "end": v(29.35, -18.98) * mm});
            skArc(sketch, "E549", {"start": v(29.93, -26.55) * mm, "mid": v(32.68, -24.91) * mm, "end": v(35.8, -24.2) * mm});
            skLineSegment(sketch, "E550", {"start": v(27.89, -18.98) * mm, "end": v(26.83, -17.13) * mm});
            skLineSegment(sketch, "E551", {"start": v(29.35, -18.98) * mm, "end": v(27.89, -18.98) * mm});
            skArc(sketch, "E552", {"start": v(23.78, -17.13) * mm, "mid": v(22.46, -18.83) * mm, "end": v(20.38, -18.26) * mm});
            skLineSegment(sketch, "E553", {"start": v(18.27, -19.5) * mm, "end": v(20.38, -18.26) * mm});
            skArc(sketch, "E554", {"start": v(-43.52, -7.97) * mm, "mid": v(-50.37, -11.82) * mm, "end": v(-57.92, -14) * mm});
            skLineSegment(sketch, "E555", {"start": v(-26.83, -17.13) * mm, "end": v(-23.78, -17.13) * mm});
            skLineSegment(sketch, "E556", {"start": v(-35.8, -24.2) * mm, "end": v(-35.8, -20.36) * mm});
            skLineSegment(sketch, "E557", {"start": v(-21.46, -26.55) * mm, "end": v(-29.93, -26.55) * mm});
            skLineSegment(sketch, "E558", {"start": v(-18.27, -19.5) * mm, "end": v(-21.46, -26.55) * mm});
            skLineSegment(sketch, "E559", {"start": v(-16.06, -22.6) * mm, "end": v(-10.12, -18.13) * mm});
            skLineSegment(sketch, "E560", {"start": v(-16.06, -27.48) * mm, "end": v(-16.06, -22.6) * mm});
            skLineSegment(sketch, "E561", {"start": v(-22.21, -31.67) * mm, "end": v(-16.06, -27.48) * mm});
            skLineSegment(sketch, "E562", {"start": v(-22.21, -36.09) * mm, "end": v(-22.21, -31.67) * mm});
            skLineSegment(sketch, "E563", {"start": v(-25.51, -39.91) * mm, "end": v(-22.21, -36.09) * mm});
            skLineSegment(sketch, "E564", {"start": v(-25.51, -45.15) * mm, "end": v(-25.51, -39.91) * mm});
            skLineSegment(sketch, "E565", {"start": v(-24.6, -46.35) * mm, "end": v(-25.51, -45.15) * mm});
            skLineSegment(sketch, "E566", {"start": v(-22.14, -46.35) * mm, "end": v(-24.6, -46.35) * mm});
            skLineSegment(sketch, "E567", {"start": v(-19.36, -44.6) * mm, "end": v(-22.14, -46.35) * mm});
            skLineSegment(sketch, "E568", {"start": v(-12.5, -34.26) * mm, "end": v(-19.36, -44.6) * mm});
            skLineSegment(sketch, "E569", {"start": v(-12.5, -26.3) * mm, "end": v(-12.5, -34.26) * mm});
            skLineSegment(sketch, "E570", {"start": v(-4.73, -26.3) * mm, "end": v(-12.5, -26.3) * mm});
            skLineSegment(sketch, "E571", {"start": v(-2.9, -29.05) * mm, "end": v(-4.73, -26.3) * mm});
            skLineSegment(sketch, "E572", {"start": v(-2.9, -31.88) * mm, "end": v(-2.9, -29.05) * mm});
            skLineSegment(sketch, "E573", {"start": v(-13.24, -44.96) * mm, "end": v(-2.9, -31.88) * mm});
            skLineSegment(sketch, "E574", {"start": v(-13.24, -52.3) * mm, "end": v(-13.24, -44.96) * mm});
            skLineSegment(sketch, "E575", {"start": v(-6.9, -52.3) * mm, "end": v(-13.24, -52.3) * mm});
            skLineSegment(sketch, "E576", {"start": v(-2.53, -42.5) * mm, "end": v(-6.9, -52.3) * mm});
            skLineSegment(sketch, "E577", {"start": v(-2.53, -34.89) * mm, "end": v(-2.53, -42.5) * mm});
            skLineSegment(sketch, "E578", {"start": v(-1.43, -33.9) * mm, "end": v(-2.53, -34.89) * mm});
            skLineSegment(sketch, "E579", {"start": v(0, -34.76) * mm, "end": v(-1.43, -33.9) * mm});
            skArc(sketch, "E580", {"start": v(-12.38, -60.6) * mm, "mid": v(-6.8, -56.73) * mm, "end": v(0, -56.53) * mm});
            skLineSegment(sketch, "E581", {"start": v(-12.38, -60.6) * mm, "end": v(-14.35, -59.08) * mm});
            skArc(sketch, "E582", {"start": v(-14.35, -59.08) * mm, "mid": v(-17.41, -58.47) * mm, "end": v(-19.15, -61.07) * mm});
            skLineSegment(sketch, "E583", {"start": v(-19.15, -64.6) * mm, "end": v(-19.15, -61.07) * mm});
            skLineSegment(sketch, "E584", {"start": v(-23.69, -67.83) * mm, "end": v(-19.15, -64.6) * mm});
            skLineSegment(sketch, "E585", {"start": v(-23.69, -72.14) * mm, "end": v(-23.69, -67.83) * mm});
            skLineSegment(sketch, "E586", {"start": v(-23.69, -73.76) * mm, "end": v(-23.69, -72.14) * mm});
            skLineSegment(sketch, "E587", {"start": v(-28.35, -78.13) * mm, "end": v(-28.35, -76.22) * mm});
            skLineSegment(sketch, "E588", {"start": v(-35.52, -73.8) * mm, "end": v(-38, -76.22) * mm});
            skLineSegment(sketch, "E589", {"start": v(-35.52, -66.22) * mm, "end": v(-35.52, -73.8) * mm});
            skLineSegment(sketch, "E590", {"start": v(-29.84, -66.22) * mm, "end": v(-35.52, -66.22) * mm});
            skLineSegment(sketch, "E591", {"start": v(-29.84, -61.92) * mm, "end": v(-29.84, -66.22) * mm});
            skLineSegment(sketch, "E592", {"start": v(-24.3, -54.15) * mm, "end": v(-29.84, -61.92) * mm});
            skLineSegment(sketch, "E593", {"start": v(-24.3, -51.69) * mm, "end": v(-24.3, -54.15) * mm});
            skLineSegment(sketch, "E594", {"start": v(-30.23, -49.55) * mm, "end": v(-24.3, -51.69) * mm});
            skLineSegment(sketch, "E595", {"start": v(-28.35, -76.22) * mm, "end": v(-23.69, -73.76) * mm});
            skLineSegment(sketch, "E596", {"start": v(-33.38, -85.3) * mm, "end": v(-28.35, -78.13) * mm});
            skLineSegment(sketch, "E597", {"start": v(-38, -82.06) * mm, "end": v(-33.38, -85.3) * mm});
            skLineSegment(sketch, "E598", {"start": v(-38, -76.22) * mm, "end": v(-38, -82.06) * mm});
            skLineSegment(sketch, "E599", {"start": v(-30.23, -43.62) * mm, "end": v(-30.23, -49.55) * mm});
            skArc(sketch, "E600", {"start": v(-30.23, -30.92) * mm, "mid": v(-27.76, -37.27) * mm, "end": v(-30.23, -43.62) * mm});
            skArc(sketch, "E601", {"start": v(-45.89, -24.16) * mm, "mid": v(-37.82, -26.99) * mm, "end": v(-30.23, -30.92) * mm});
            skLineSegment(sketch, "E602", {"start": v(-45.89, -17.18) * mm, "end": v(-45.89, -24.16) * mm});
            skArc(sketch, "E603", {"start": v(-50.5, -21.87) * mm, "mid": v(-49.39, -18.35) * mm, "end": v(-45.89, -17.18) * mm});
            skLineSegment(sketch, "E604", {"start": v(-50.5, -21.87) * mm, "end": v(-52.56, -21.87) * mm});
            skArc(sketch, "E605", {"start": v(-55.36, -17.28) * mm, "mid": v(-53, -18.99) * mm, "end": v(-52.56, -21.87) * mm});
            skLineSegment(sketch, "E606", {"start": v(-57.69, -20.46) * mm, "end": v(-55.36, -17.28) * mm});
            skLineSegment(sketch, "E607", {"start": v(-60.38, -20.46) * mm, "end": v(-57.69, -20.46) * mm});
            skLineSegment(sketch, "E608", {"start": v(-62.45, -17.28) * mm, "end": v(-60.38, -20.46) * mm});
            skArc(sketch, "E609", {"start": v(-76.2, -15.34) * mm, "mid": v(-69.43, -17.02) * mm, "end": v(-62.45, -17.28) * mm});
            skLineSegment(sketch, "E610", {"start": v(-58.87, -10.56) * mm, "end": v(-76.2, -15.34) * mm});
            skLineSegment(sketch, "E611", {"start": v(-57.92, -14) * mm, "end": v(-58.87, -10.56) * mm});
            skLineSegment(sketch, "E612", {"start": v(-43.52, -13.51) * mm, "end": v(-43.52, -7.97) * mm});
            skLineSegment(sketch, "E613", {"start": v(-18.27, -19.5) * mm, "end": v(-20.38, -18.26) * mm});
            skArc(sketch, "E614", {"start": v(-9.72, -15) * mm, "mid": v(-26.66, -15.14) * mm, "end": v(-43.52, -13.51) * mm});
            skLineSegment(sketch, "E615", {"start": v(-10.12, -18.13) * mm, "end": v(-9.72, -15) * mm});
            skArc(sketch, "E616", {"start": v(-23.78, -17.13) * mm, "mid": v(-22.46, -18.83) * mm, "end": v(-20.38, -18.26) * mm});
            skLineSegment(sketch, "E617", {"start": v(-27.89, -18.98) * mm, "end": v(-26.83, -17.13) * mm});
            skLineSegment(sketch, "E618", {"start": v(-29.35, -18.98) * mm, "end": v(-27.89, -18.98) * mm});
            skArc(sketch, "E619", {"start": v(-35.8, -20.36) * mm, "mid": v(-32.8, -18.58) * mm, "end": v(-29.35, -18.98) * mm});
            skArc(sketch, "E620", {"start": v(-29.93, -26.55) * mm, "mid": v(-32.68, -24.91) * mm, "end": v(-35.8, -24.2) * mm});
            skLineSegment(sketch, "E621", {"start": v(0, 0) * mm, "end": v(0, -90.94) * mm, "construction": true});
            skSolve(sketch);
        }
        {
            var Q0;
            Q0=makeQuery(id+"F6.imprint","IMPRINT",FACE,{"disambiguationData":[TD([[makeQuery(id+"F6.imprint","IMPRINT",EDGE,{"derivedFrom":sQuery(id+"F6.wireOp",EDGE,"E9")}),-1.0]])]});
            extrude(context, id + "F7", {"entities" : qUnion([Q0]), "operationType" : NewBodyOperationType.ADD, "oppositeDirection" : true, "depth" : 6.35 * mm, "offsetDistance" : 25.4 * mm});
        }
        {
            var Q0;
            Q0 = qSketchRegion(id + "F6", true);
            extrude(context, id + "F8", {"entities" : qUnion([Q0]), "operationType" : NewBodyOperationType.ADD, "depth" : 3.17 * mm, "offsetDistance" : 25.4 * mm});
        }
    });
